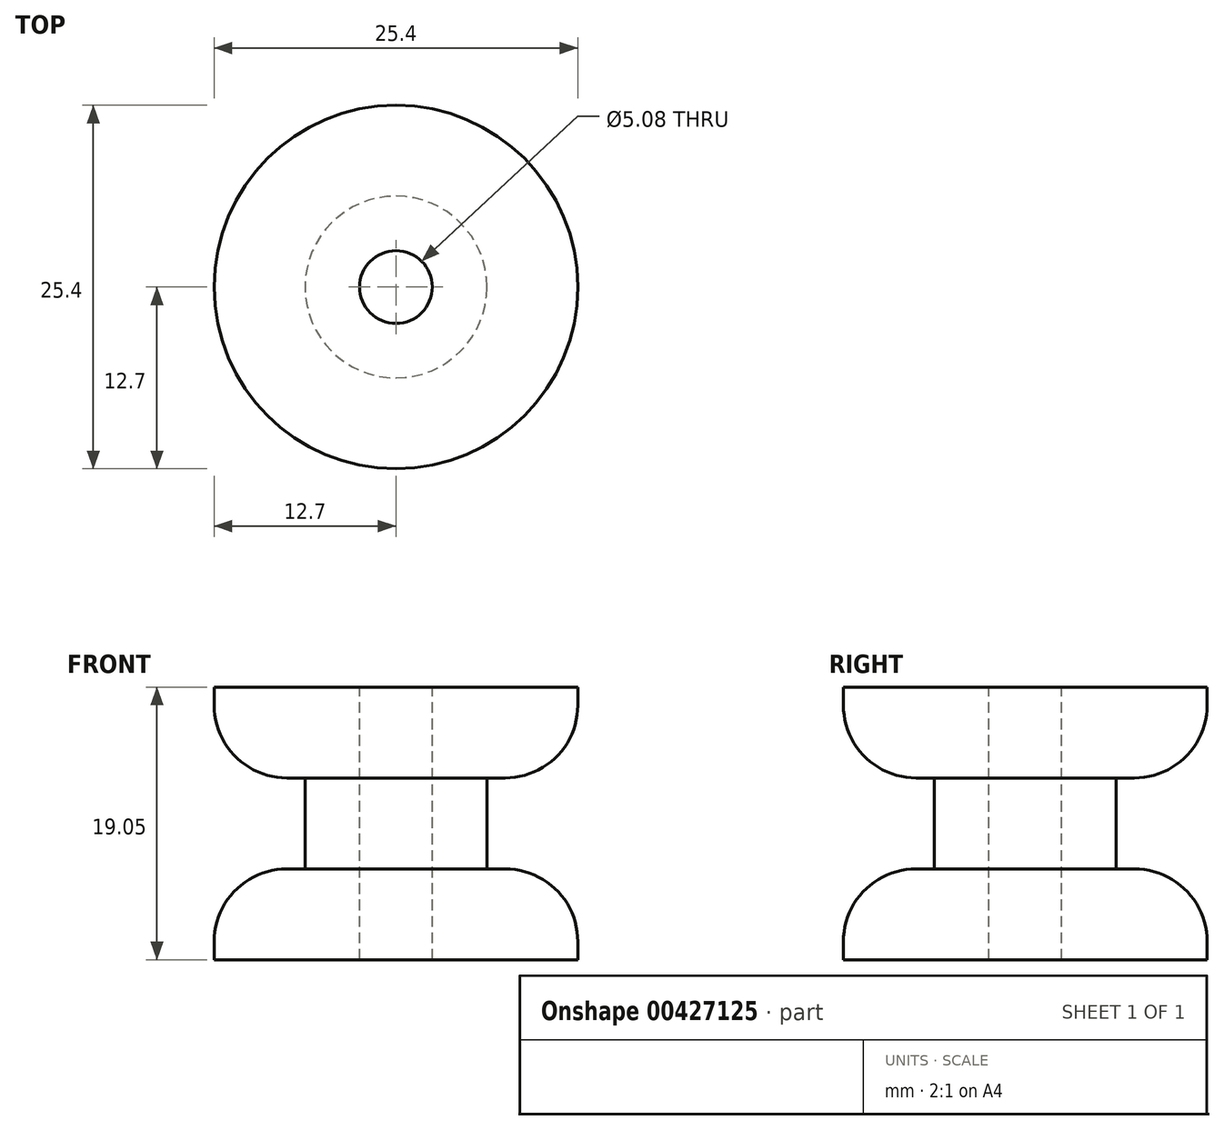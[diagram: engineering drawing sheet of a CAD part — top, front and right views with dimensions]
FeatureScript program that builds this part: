
annotation { "Feature Type Name" : "Feature", "Feature Type Description" : "" }
export const myFeature = defineFeature(function(context is Context, id is Id, definition is map)
    precondition{}
    {
        {
            var Q0;
            Q0=qCreatedBy(makeId("Top.planeOp"),FACE);
            var sketch = newSketch(context, id + "F0", { "sketchPlane" : qUnion([Q0])});
            skCircle(sketch, "E0", {"center": v(0, 0) * mm, "radius": 12.7 * mm});
            skSolve(sketch);
        }
        {
            var Q0;
            Q0=makeQuery(id+"F0.imprint","IMPRINT",FACE,{"disambiguationData":[TD([[makeQuery(id+"F0.imprint","IMPRINT",EDGE,{"derivedFrom":sQuery(id+"F0.wireOp",EDGE,"E0")}),1.0]])]});
            extrude(context, id + "F1", {"entities" : qUnion([Q0]), "depth" : 6.35 * mm});
        }
        {
            var Q0;
            Q0=makeQuery(id+"F1.opExtrude","CAP_FACE",FACE,{"disambiguationData":[OSD([sQuery(id+"F0.wireOp",EDGE,"E0")])],"isStart":false});
            var sketch = newSketch(context, id + "F2", { "sketchPlane" : qUnion([Q0])});
            skCircle(sketch, "E1", {"center": v(0, 0) * mm, "radius": 6.35 * mm});
            skSolve(sketch);
        }
        {
            var Q0;
            Q0=makeQuery(id+"F2.imprint","IMPRINT",FACE,{"disambiguationData":[TD([[makeQuery(id+"F2.imprint","IMPRINT",EDGE,{"derivedFrom":sQuery(id+"F2.wireOp",EDGE,"E1")}),1.0]])]});
            extrude(context, id + "F3", {"entities" : qUnion([Q0]), "operationType" : NewBodyOperationType.ADD, "depth" : 6.35 * mm});
        }
        {
            var Q0;
            Q0=makeQuery(id+"F3.opExtrude","CAP_FACE",FACE,{"disambiguationData":[OSD([sQuery(id+"F2.wireOp",EDGE,"E1")])],"isStart":false});
            var sketch = newSketch(context, id + "F4", { "sketchPlane" : qUnion([Q0])});
            skCircle(sketch, "E2", {"center": v(0, 0) * mm, "radius": 12.7 * mm});
            skSolve(sketch);
        }
        {
            var Q0;
            Q0=makeQuery(id+"F4.imprint","IMPRINT",FACE,{"disambiguationData":[TD([[makeQuery(id+"F4.imprint","IMPRINT",EDGE,{"derivedFrom":sQuery(id+"F4.wireOp",EDGE,"E2")}),1.0]])]});
            var Q1;
            Q1=makeQuery(id+"F4.imprint","IMPRINT",FACE,{"disambiguationData":[TD([[makeQuery(id+"F4.imprint","IMPRINT",EDGE,{"derivedFrom":makeQuery(id+"F3.opExtrude","CAP_EDGE",EDGE,{"disambiguationData":[OSD([sQuery(id+"F2.wireOp",EDGE,"E1")])],"isStart":false})}),1.0]])]});
            extrude(context, id + "F5", {"entities" : qUnion([Q0, Q1]), "operationType" : NewBodyOperationType.ADD, "depth" : 6.35 * mm});
        }
        {
            var Q0;
            Q0=makeQuery(id+"F5.opExtrude","CAP_FACE",FACE,{"disambiguationData":[OSD([sQuery(id+"F4.wireOp",EDGE,"E2")])],"isStart":false});
            var sketch = newSketch(context, id + "F6", { "sketchPlane" : qUnion([Q0])});
            skCircle(sketch, "E3", {"center": v(0, 0) * mm, "radius": 2.54 * mm});
            skSolve(sketch);
        }
        {
            var Q0;
            Q0=makeQuery(id+"F6.imprint","IMPRINT",FACE,{"disambiguationData":[TD([[makeQuery(id+"F6.imprint","IMPRINT",EDGE,{"derivedFrom":sQuery(id+"F6.wireOp",EDGE,"E3")}),1.0]])]});
            extrude(context, id + "F7", {"entities" : qUnion([Q0]), "operationType" : NewBodyOperationType.REMOVE, "oppositeDirection" : true, "depth" : 19.05 * mm});
        }
        {
            var Q0;
            Q0=makeQuery(id+"F5.opExtrude","CAP_EDGE",EDGE,{"disambiguationData":[OSD([sQuery(id+"F4.wireOp",EDGE,"E2")])],"isStart":true});
            var Q1;
            Q1=makeQuery(id+"F1.opExtrude","CAP_EDGE",EDGE,{"disambiguationData":[OSD([sQuery(id+"F0.wireOp",EDGE,"E0")])],"isStart":false});
            fillet(context, id + "F8", {"entities" : qUnion([Q0, Q1]), "radius" : 5.08 * mm, "tangentPropagation" : true, "allowEdgeOverflow" : false});
        }
    });
